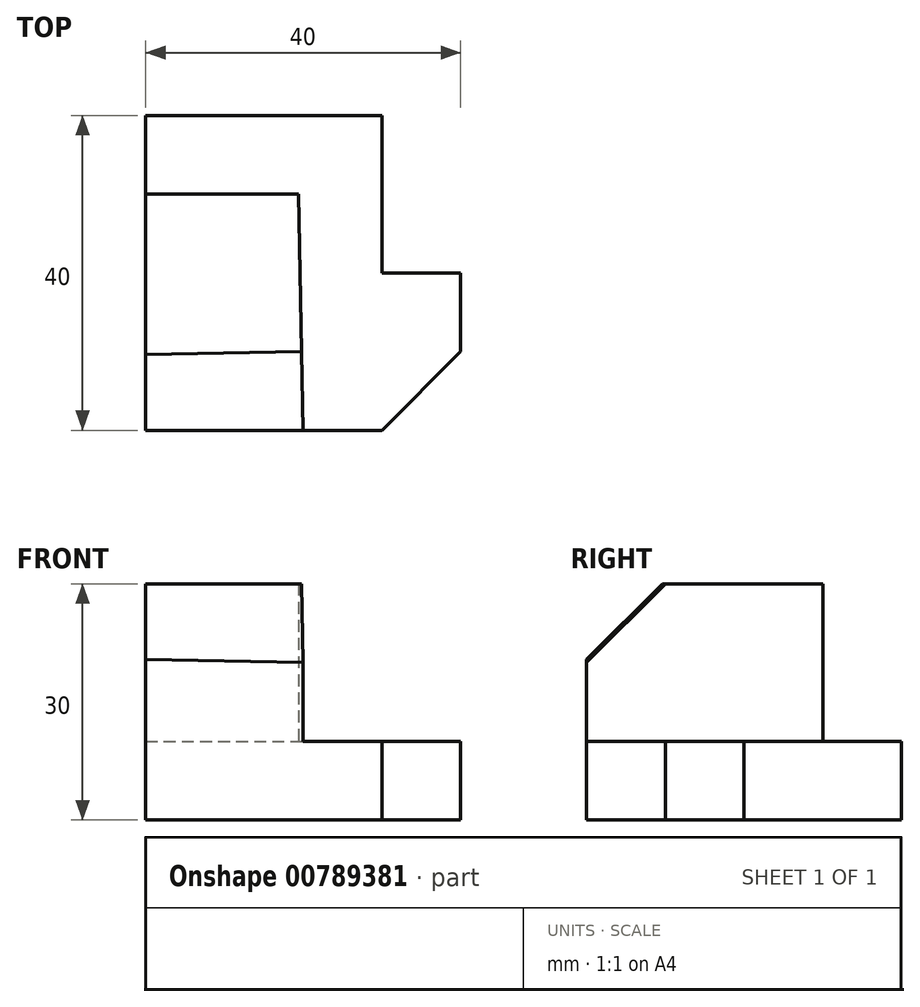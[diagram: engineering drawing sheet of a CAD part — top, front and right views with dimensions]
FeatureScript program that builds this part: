
annotation { "Feature Type Name" : "Feature", "Feature Type Description" : "" }
export const myFeature = defineFeature(function(context is Context, id is Id, definition is map)
    precondition{}
    {
        {
            var Q0;
            Q0=qCreatedBy(makeId("Top.planeOp"),FACE);
            var sketch = newSketch(context, id + "F0", { "sketchPlane" : qUnion([Q0])});
            skLineSegment(sketch, "E0", {"start": v(0, 40) * mm, "end": v(0, 0) * mm});
            skLineSegment(sketch, "E1", {"start": v(0, 40) * mm, "end": v(30, 40) * mm});
            skLineSegment(sketch, "E2", {"start": v(30, 20) * mm, "end": v(30, 40) * mm});
            skLineSegment(sketch, "E3", {"start": v(40, 20) * mm, "end": v(30, 20) * mm});
            skLineSegment(sketch, "E4", {"start": v(40, 10) * mm, "end": v(40, 20) * mm});
            skLineSegment(sketch, "E5", {"start": v(30, 0) * mm, "end": v(0, 0) * mm});
            skLineSegment(sketch, "E6", {"start": v(30, 0) * mm, "end": v(40, 10) * mm});
            skSolve(sketch);
        }
        {
            var Q0;
            Q0 = qSketchRegion(id + "F0", true);
            extrude(context, id + "F1", {"entities" : qUnion([Q0]), "depth" : 10 * mm, "offsetDistance" : 25 * mm});
        }
        {
            var Q0;
            Q0=makeQuery(id+"F1.opExtrude","CAP_FACE",FACE,{"disambiguationData":[OSD([sQuery(id+"F0.wireOp",EDGE,"E0"),sQuery(id+"F0.wireOp",EDGE,"E1"),sQuery(id+"F0.wireOp",EDGE,"E2"),sQuery(id+"F0.wireOp",EDGE,"E3"),sQuery(id+"F0.wireOp",EDGE,"E4"),sQuery(id+"F0.wireOp",EDGE,"E5"),sQuery(id+"F0.wireOp",EDGE,"E6")])],"isStart":false});
            var sketch = newSketch(context, id + "F2", { "sketchPlane" : qUnion([Q0])});
            skLineSegment(sketch, "E7", {"start": v(0, 30) * mm, "end": v(0, 0) * mm});
            skLineSegment(sketch, "E8", {"start": v(20, 0) * mm, "end": v(0, 0) * mm});
            skLineSegment(sketch, "E9", {"start": v(19.44, 30) * mm, "end": v(20, 0) * mm});
            skLineSegment(sketch, "E10", {"start": v(0, 30) * mm, "end": v(19.44, 30) * mm});
            skSolve(sketch);
        }
        {
            var Q0;
            Q0 = qSketchRegion(id + "F2", true);
            extrude(context, id + "F3", {"entities" : qUnion([Q0]), "operationType" : NewBodyOperationType.ADD, "depth" : 20 * mm, "offsetDistance" : 25 * mm});
        }
        {
            var Q0;
            Q0=makeQuery(id+"F3.opExtrude","SWEPT_FACE",FACE,{"disambiguationData":[OSD([sQuery(id+"F2.wireOp",EDGE,"E9")])]});
            var sketch = newSketch(context, id + "F4", { "sketchPlane" : qUnion([Q0])});
            skLineSegment(sketch, "E11", {"start": v(-0.38, 30) * mm, "end": v(9.62, 30) * mm});
            skLineSegment(sketch, "E12", {"start": v(-0.38, 30) * mm, "end": v(-0.38, 20) * mm});
            skLineSegment(sketch, "E13", {"start": v(-0.38, 20) * mm, "end": v(9.62, 30) * mm});
            skSolve(sketch);
        }
        {
            var Q0;
            Q0 = qSketchRegion(id + "F4", true);
            extrude(context, id + "F5", {"entities" : qUnion([Q0]), "operationType" : NewBodyOperationType.REMOVE, "oppositeDirection" : true, "depth" : 25 * mm, "offsetDistance" : 25 * mm});
        }
    });
